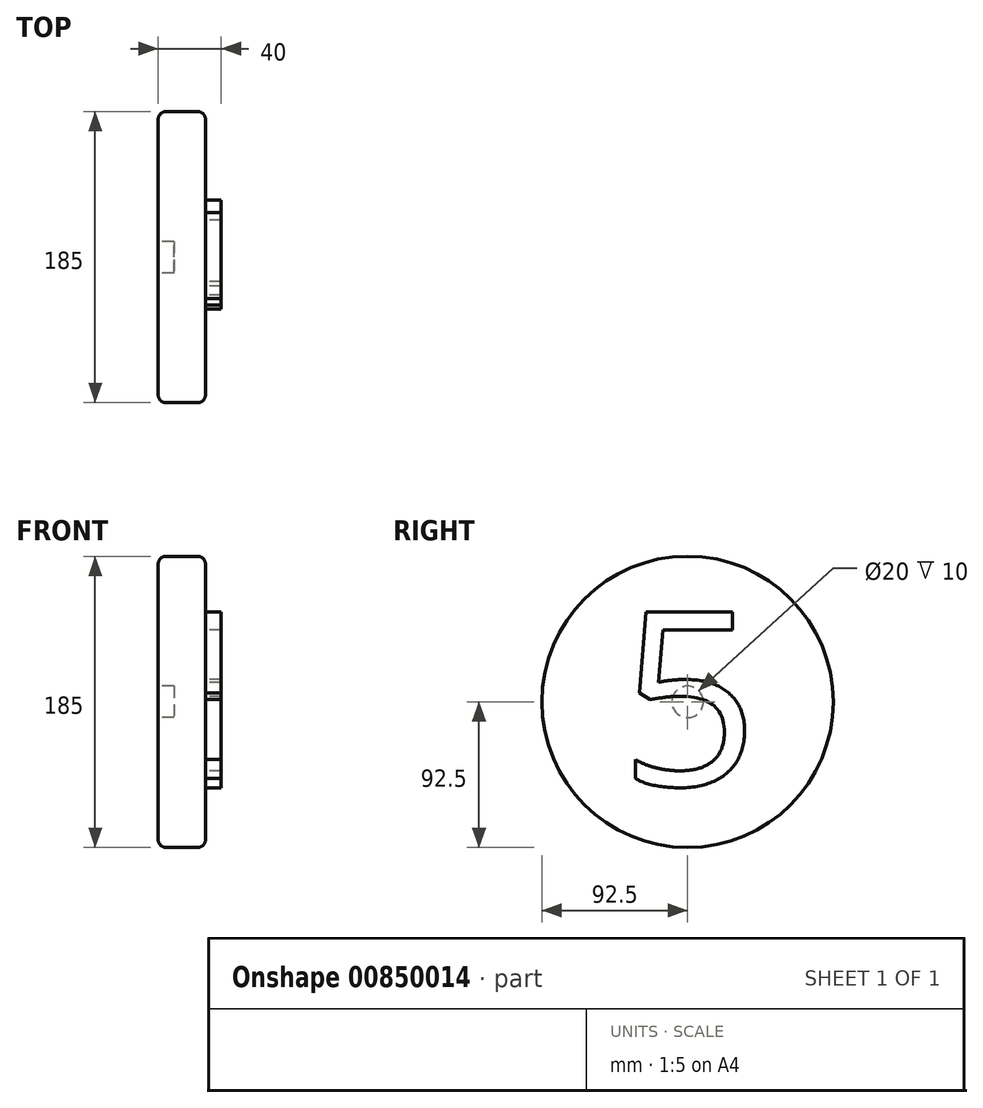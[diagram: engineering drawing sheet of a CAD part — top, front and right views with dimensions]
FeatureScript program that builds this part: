
annotation { "Feature Type Name" : "Feature", "Feature Type Description" : "" }
export const myFeature = defineFeature(function(context is Context, id is Id, definition is map)
    precondition{}
    {
        {
            var Q0;
            Q0=qCreatedBy(makeId("Right.planeOp"),FACE);
            var sketch = newSketch(context, id + "F0", { "sketchPlane" : qUnion([Q0])});
            skCircle(sketch, "E0", {"center": v(0, 0) * mm, "radius": 92.5 * mm});
            skSolve(sketch);
        }
        {
            var Q0;
            Q0=makeQuery(id+"F0.imprint","IMPRINT",FACE,{"disambiguationData":[TD([[makeQuery(id+"F0.imprint","IMPRINT",EDGE,{"derivedFrom":sQuery(id+"F0.wireOp",EDGE,"E0")}),1.0]])]});
            extrude(context, id + "F1", {"entities" : qUnion([Q0]), "depth" : 30 * mm, "offsetDistance" : 25 * mm});
        }
        {
            var Q0;
            Q0=makeQuery(id+"F1.opExtrude","CAP_FACE",FACE,{"disambiguationData":[OSD([sQuery(id+"F0.wireOp",EDGE,"E0")])],"isStart":true});
            var sketch = newSketch(context, id + "F2", { "sketchPlane" : qUnion([Q0])});
            skCircle(sketch, "E1", {"center": v(0, 0) * mm, "radius": 10 * mm});
            skSolve(sketch);
        }
        {
            var Q0;
            Q0=makeQuery(id+"F2.imprint","IMPRINT",FACE,{"disambiguationData":[TD([[makeQuery(id+"F2.imprint","IMPRINT",EDGE,{"derivedFrom":sQuery(id+"F2.wireOp",EDGE,"E1")}),1.0]])]});
            extrude(context, id + "F3", {"entities" : qUnion([Q0]), "operationType" : NewBodyOperationType.REMOVE, "oppositeDirection" : true, "depth" : 10 * mm, "offsetDistance" : 25 * mm});
        }
        {
            var Q0;
            Q0=makeQuery(id+"F1.opExtrude","CAP_FACE",FACE,{"disambiguationData":[OSD([sQuery(id+"F0.wireOp",EDGE,"E0")])],"isStart":false});
            var sketch = newSketch(context, id + "F4", { "sketchPlane" : qUnion([Q0])});
            skText(sketch, "E2", { "text": "5\n", "fontName": "OpenSans-Regular.ttf"});
            const initialGuessF4  = {"E2": [-0.04313, -0.05306, 1, 0, 0.11108]};
            skSetInitialGuess(sketch, initialGuessF4);
            skSolve(sketch);
        }
        {
            var Q0;
            Q0 = qSketchRegion(id + "F4", true);
            extrude(context, id + "F5", {"entities" : qUnion([Q0]), "operationType" : NewBodyOperationType.ADD, "depth" : 10 * mm, "offsetDistance" : 25 * mm});
        }
        {
            var Q0;
            Q0=makeQuery(id+"F1.opExtrude","CAP_EDGE",EDGE,{"disambiguationData":[OSD([sQuery(id+"F0.wireOp",EDGE,"E0")])],"isStart":false});
            var Q1;
            Q1=makeQuery(id+"F1.opExtrude","CAP_EDGE",EDGE,{"disambiguationData":[OSD([sQuery(id+"F0.wireOp",EDGE,"E0")])],"isStart":true});
            fillet(context, id + "F6", {"entities" : qUnion([Q0, Q1]), "radius" : 5 * mm, "tangentPropagation" : true, "allowEdgeOverflow" : false});
        }
    });
